# Revit family: 937590001_Sifon Botella Flexible Doble
name_source: partatom
category: Plumbing Fixtures
units: mm (PartAtom-declared; Revit-internal decimal feet)

## family parameters
Always vertical = Yes
Cut with Voids When Loaded = No
OmniClass Number = 23.27.43.00
OmniClass Title = Pipe Fittings
Part Type = Normal
Room Calculation Point = No
Round Connector Dimension = Use Diameter
Shared = No
Work Plane-Based = No

## types (1)
- 937590001_Sifon Botella Flexible Doble
    Alto = 478.6 mm  [stored 1.57021 ft]
    Ancho = 542.4 mm
    Capacidad de evacuación = 27 lts/min.
    Creado por = BIMBAU
    Cuidado Y Limpieza = Los acabados superficiales son aquellos que le imprimen una 
apariencia especial y estética a su producto y además le brindan 
protección. Para prolongar sus cualidades es vital que la limpieza 
profunda del producto se haga únicamente con agua y jabón 
suave y que en el secado y el brillo se utilice un paño de algodón 
limpio; dicha limpieza se recomienda 2 veces a la semana y en 
zonas costeras a diario por la salinidad del ambiente. Por ningún 
motivo deben usarse elementos abrasivos, ácidos o disolventes 
para la limpieza del producto. Los acabados pueden variar su 
comportamiento en zonas costeras y/o en ambientes corrosivos.
    Default Elevation = 0 mm  [stored 0 ft]
    Description = -Fácil proceso de instalación. -Material en plastico de alta resistencia y duralibilidad. -Funciona para doble poceta.
    Fecha de creación = 09/04/2021
    Longitud = 815.1 mm
    Manufacturer = Grival
    Material = Corona_Plastico_Gris
    Model = Sifón Botella Flexible Doble Gris
    Normatividad = NTC 5302
    Peso Bruto aprox = 675gr. - 1,49lb.
    Peso Neto aprox = 515gr. - 1,14lb.
    Referencia = 937590001
    URL = https://www.grival.com

note: [stored X ft] marks values corroborated as IEEE doubles in the binary element streams (Revit-internal decimal feet)

## geometry (parser evidence)
native form markers: Sweep x5
no freeform markers — native parametric forms only
